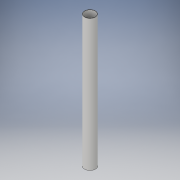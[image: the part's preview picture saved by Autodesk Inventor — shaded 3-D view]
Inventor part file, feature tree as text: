
AUTODESK INVENTOR PART (.ipt)
format: ipt  version: 2017 (Build 210142000, 142)  size: 92,672 bytes
history: native  units: in
note: dims shown in document units (in); Inventor stores cm internally (conversion verified against a paired STEP export)
features: extrude x1, sketch x1
ambient origin geometry x8: Origin, YZ Plane, XZ Plane, XY Plane, X Axis, Y Axis, Z Axis, Center Point
bodies: Solid1 (feature_tree)
feature tree (2):
  extrude  "Extrusion1"  Depth=24.0in
  sketch  "Sketch1"  dims[d0=2.0in d1=1.875in d2=24.0in d3=0.0in]
